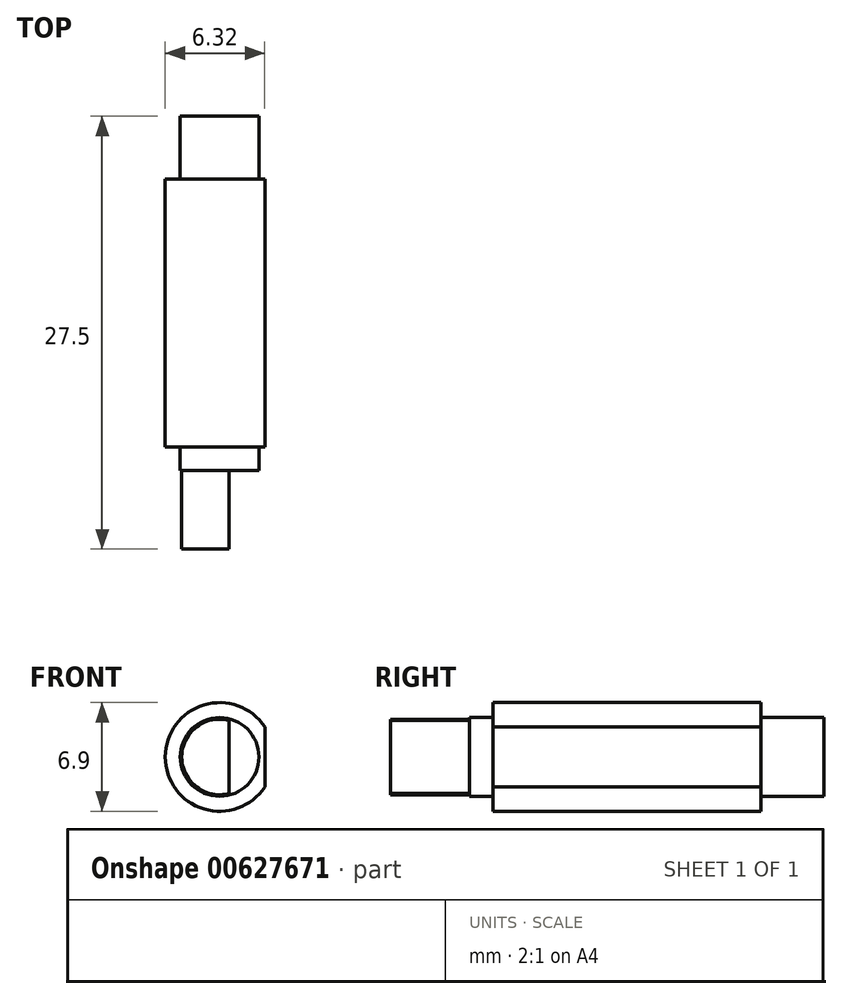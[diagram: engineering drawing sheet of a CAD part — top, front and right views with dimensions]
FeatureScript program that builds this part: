
annotation { "Feature Type Name" : "Feature", "Feature Type Description" : "" }
export const myFeature = defineFeature(function(context is Context, id is Id, definition is map)
    precondition{}
    {
        {
            var Q0;
            Q0=qCreatedBy(makeId("Front.planeOp"),FACE);
            var sketch = newSketch(context, id + "F0", { "sketchPlane" : qUnion([Q0])});
            skArc(sketch, "E0", {"start": v(3.17, 2) * mm, "mid": v(-3.75, 0) * mm, "end": v(3.17, -2) * mm, "construction": true});
            skLineSegment(sketch, "E1", {"start": v(3.17, 2) * mm, "end": v(3.17, -2) * mm, "construction": true});
            skArc(sketch, "E2.0", {"start": v(2.87, 1.91) * mm, "mid": v(-3.45, 0) * mm, "end": v(2.87, -1.91) * mm});
            skLineSegment(sketch, "E2.1", {"start": v(2.87, 1.91) * mm, "end": v(2.87, -1.91) * mm});
            skSolve(sketch);
        }
        {
            var Q0;
            Q0 = qSketchRegion(id + "F0", true);
            extrude(context, id + "F1", {"entities" : qUnion([Q0]), "depth" : 17 * mm, "offsetDistance" : 25 * mm});
        }
        {
            var Q0;
            Q0=makeQuery(id+"F1.opExtrude","CAP_FACE",FACE,{"disambiguationData":[OSD([sQuery(id+"F0.wireOp",EDGE,"E2.0"),sQuery(id+"F0.wireOp",EDGE,"E2.1")])],"isStart":false});
            var sketch = newSketch(context, id + "F2", { "sketchPlane" : qUnion([Q0])});
            skCircle(sketch, "E3", {"center": v(0, 0) * mm, "radius": 3 * mm, "construction": true});
            skCircle(sketch, "E4.0", {"center": v(0, 0) * mm, "radius": 2.5 * mm});
            skSolve(sketch);
        }
        {
            var Q0;
            Q0 = qSketchRegion(id + "F2", true);
            extrude(context, id + "F3", {"entities" : qUnion([Q0]), "operationType" : NewBodyOperationType.ADD, "depth" : 1.5 * mm, "offsetDistance" : 25 * mm});
        }
        {
            var Q0;
            Q0=makeQuery(id+"F1.opExtrude","CAP_FACE",FACE,{"disambiguationData":[OSD([sQuery(id+"F0.wireOp",EDGE,"E2.0"),sQuery(id+"F0.wireOp",EDGE,"E2.1")])],"isStart":true});
            var sketch = newSketch(context, id + "F4", { "sketchPlane" : qUnion([Q0])});
            skCircle(sketch, "E5", {"center": v(0, 0) * mm, "radius": 3 * mm, "construction": true});
            skCircle(sketch, "E6.0", {"center": v(0, 0) * mm, "radius": 2.5 * mm});
            skSolve(sketch);
        }
        {
            var Q0;
            Q0 = qSketchRegion(id + "F4", true);
            extrude(context, id + "F5", {"entities" : qUnion([Q0]), "operationType" : NewBodyOperationType.ADD, "depth" : 4 * mm, "offsetDistance" : 25 * mm});
        }
        {
            var Q0;
            Q0=makeQuery(id+"F3.opExtrude","CAP_FACE",FACE,{"disambiguationData":[OSD([sQuery(id+"F2.wireOp",EDGE,"E4.0")])],"isStart":false});
            var sketch = newSketch(context, id + "F6", { "sketchPlane" : qUnion([Q0])});
            skArc(sketch, "E7", {"start": v(1.1, 2.68) * mm, "mid": v(-2.9, 0) * mm, "end": v(1.1, -2.68) * mm, "construction": true});
            skLineSegment(sketch, "E8", {"start": v(1.1, 2.68) * mm, "end": v(1.1, -2.68) * mm, "construction": true});
            skArc(sketch, "E9.0", {"start": v(0.6, 2.32) * mm, "mid": v(-2.4, 0) * mm, "end": v(0.6, -2.32) * mm});
            skLineSegment(sketch, "E9.1", {"start": v(0.6, 2.32) * mm, "end": v(0.6, -2.32) * mm});
            skSolve(sketch);
        }
        {
            var Q0;
            Q0 = qSketchRegion(id + "F6", true);
            extrude(context, id + "F7", {"entities" : qUnion([Q0]), "operationType" : NewBodyOperationType.ADD, "depth" : 5 * mm, "offsetDistance" : 25 * mm});
        }
    });
